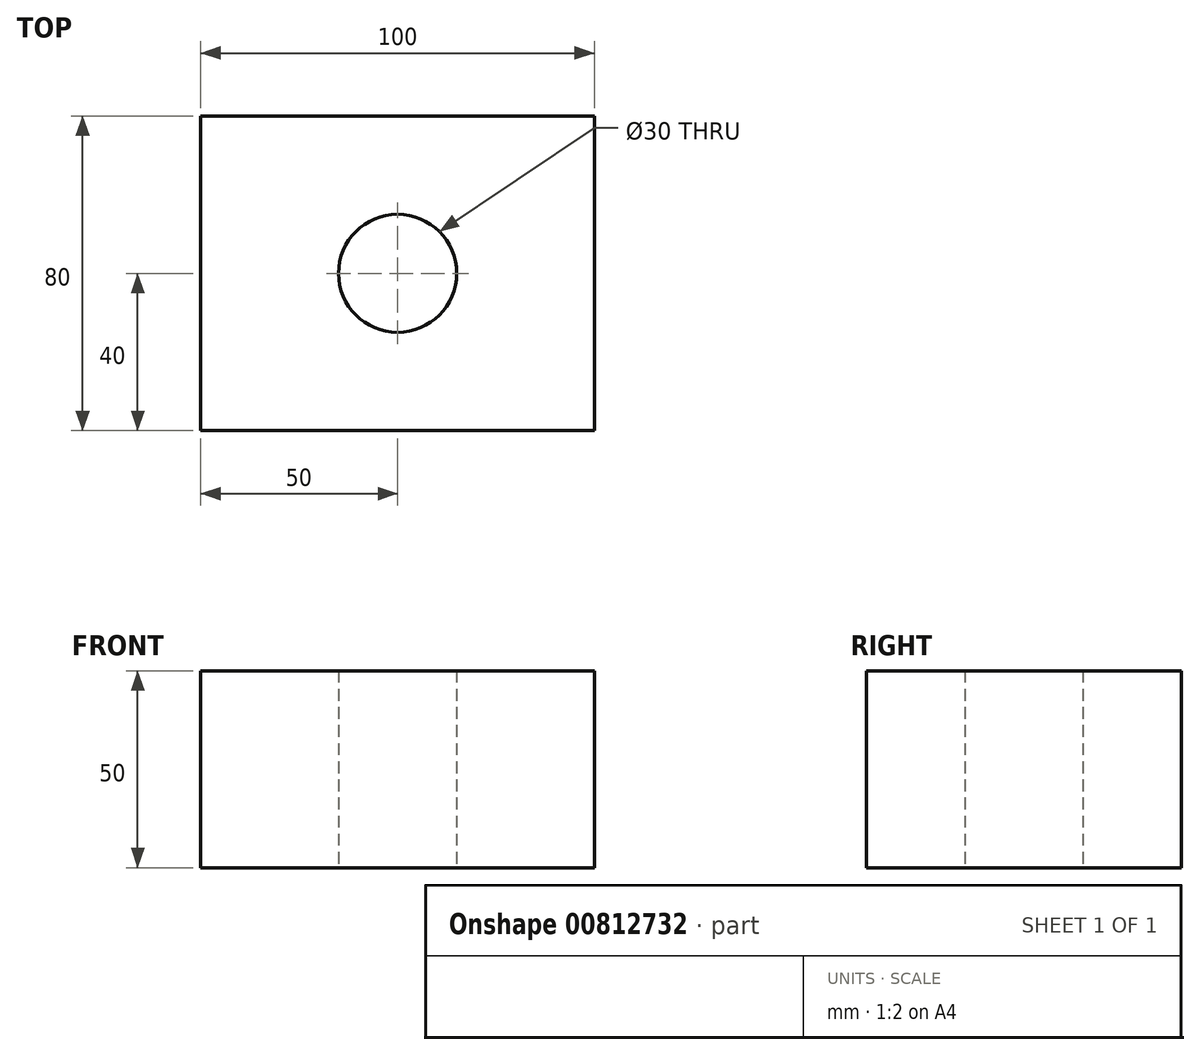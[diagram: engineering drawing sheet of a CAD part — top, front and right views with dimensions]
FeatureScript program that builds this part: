
annotation { "Feature Type Name" : "Feature", "Feature Type Description" : "" }
export const myFeature = defineFeature(function(context is Context, id is Id, definition is map)
    precondition{}
    {
        {
            var Q0;
            Q0=qCreatedBy(makeId("Top.planeOp"),FACE);
            var sketch = newSketch(context, id + "F0", { "sketchPlane" : qUnion([Q0])});
            skLineSegment(sketch, "E0.bottom", {"start": v(-50, 40) * mm, "end": v(50, 40) * mm});
            skLineSegment(sketch, "E0.top", {"start": v(-50, -40) * mm, "end": v(50, -40) * mm});
            skLineSegment(sketch, "E0.left", {"start": v(-50, 40) * mm, "end": v(-50, -40) * mm});
            skLineSegment(sketch, "E0.right", {"start": v(50, 40) * mm, "end": v(50, -40) * mm});
            skCircle(sketch, "E1", {"center": v(0, 0) * mm, "radius": 15 * mm});
            skSolve(sketch);
        }
        {
            var Q0;
            Q0=makeQuery(id+"F0.imprint","IMPRINT",FACE,{"disambiguationData":[TD([[makeQuery(id+"F0.imprint","IMPRINT",EDGE,{"derivedFrom":sQuery(id+"F0.wireOp",EDGE,"E0.bottom")}),-1.0]])]});
            extrude(context, id + "F1", {"entities" : qUnion([Q0]), "endBound" : BoundingType.SYMMETRIC, "depth" : 50 * mm, "offsetDistance" : 25 * mm});
        }
        {
            var Q0;
            Q0 = qSketchRegion(id + "F0", true);
            extrude(context, id + "F2", {"entities" : qUnion([Q0]), "operationType" : NewBodyOperationType.ADD, "depth" : 25 * mm, "offsetDistance" : 25 * mm});
        }
    });
